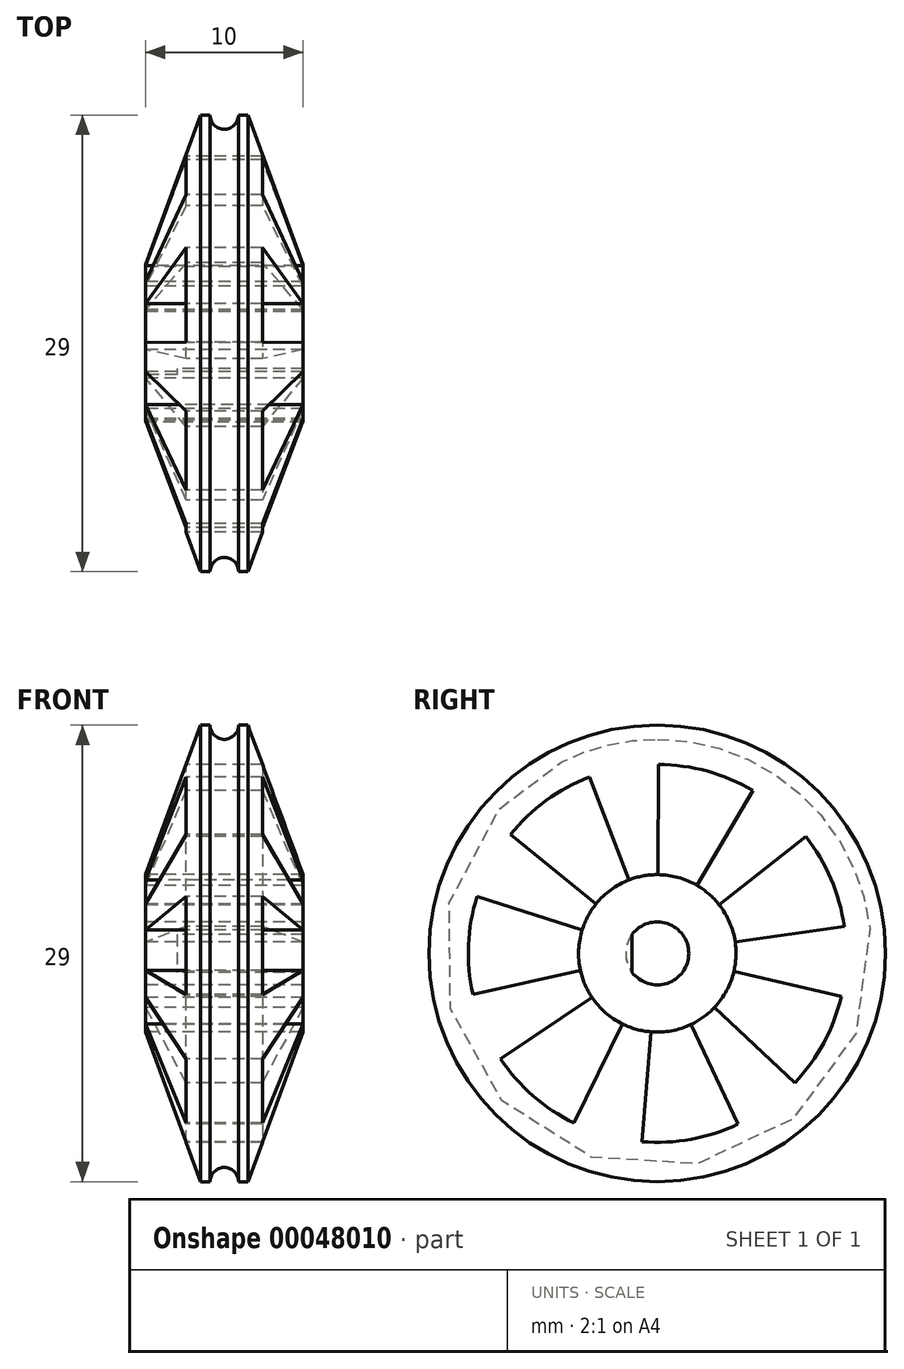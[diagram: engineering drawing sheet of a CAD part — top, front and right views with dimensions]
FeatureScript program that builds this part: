
annotation { "Feature Type Name" : "Feature", "Feature Type Description" : "" }
export const myFeature = defineFeature(function(context is Context, id is Id, definition is map)
    precondition{}
    {
        {
            var Q0;
            Q0=qCreatedBy(makeId("Front.planeOp"),FACE);
            var sketch = newSketch(context, id + "F0", { "sketchPlane" : qUnion([Q0])});
            skLineSegment(sketch, "E0.bottom", {"start": v(0, 0) * mm, "end": v(10, 0) * mm});
            skLineSegment(sketch, "E0.top", {"start": v(0, 5) * mm, "end": v(10, 5) * mm});
            skLineSegment(sketch, "E0.left", {"start": v(0, 0) * mm, "end": v(0, 5) * mm});
            skLineSegment(sketch, "E0.right", {"start": v(10, 0) * mm, "end": v(10, 5) * mm});
            skLineSegment(sketch, "E1", {"start": v(0, 5) * mm, "end": v(3.5, 14.5) * mm});
            skLineSegment(sketch, "E2", {"start": v(3.5, 14.5) * mm, "end": v(4.1, 14.5) * mm});
            skLineSegment(sketch, "E3", {"start": v(6.5, 14.5) * mm, "end": v(10, 5) * mm});
            skArc(sketch, "E4", {"start": v(4.1, 14.5) * mm, "mid": v(5, 13.6) * mm, "end": v(5.9, 14.5) * mm});
            skLineSegment(sketch, "E5.trimOffspring", {"start": v(5.9, 14.5) * mm, "end": v(6.5, 14.5) * mm});
            skLineSegment(sketch, "E6", {"start": v(4.1, 14.5) * mm, "end": v(5.9, 14.5) * mm, "construction": true});
            skSolve(sketch);
        }
        {
            var Q0;
            Q0 = qSketchRegion(id + "F0", true);
            var Q1;
            Q1=sQuery(id+"F0.wireOp",EDGE,"E0.bottom");
            revolve(context, id + "F1", {"entities" : qUnion([Q0]), "axis" : qUnion([Q1]), "revolveType" : RevolveType.FULL});
        }
        {
            var Q0;
            Q0=qCreatedBy(makeId("Right.planeOp"),FACE);
            var sketch = newSketch(context, id + "F2", { "sketchPlane" : qUnion([Q0])});
            skCircle(sketch, "E7", {"center": v(0, 0) * mm, "radius": 2 * mm});
            skSolve(sketch);
        }
        {
            var Q0;
            Q0=makeQuery(id+"F2.imprint","IMPRINT",FACE,{"disambiguationData":[TD([[makeQuery(id+"F2.imprint","IMPRINT",EDGE,{"derivedFrom":sQuery(id+"F2.wireOp",EDGE,"E7")}),1.0]])]});
            extrude(context, id + "F3", {"entities" : qUnion([Q0]), "operationType" : NewBodyOperationType.REMOVE, "depth" : 2 * mm});
        }
        {
            var Q0;
            Q0=makeQuery(id+"F1.opRevolve","SWEPT_FACE",FACE,{"disambiguationData":[OSD([sQuery(id+"F0.wireOp",EDGE,"E0.left")])]});
            var sketch = newSketch(context, id + "F4", { "sketchPlane" : qUnion([Q0])});
            skLineSegment(sketch, "E8", {"start": v(1.6, -1.2) * mm, "end": v(1.6, 1.2) * mm});
            skArc(sketch, "E9", {"start": v(1.6, 1.2) * mm, "mid": v(-2, 0) * mm, "end": v(1.6, -1.2) * mm});
            skArc(sketch, "E10", {"start": v(1.6, -1.2) * mm, "mid": v(2, 0) * mm, "end": v(1.6, 1.2) * mm, "construction": true});
            skArc(sketch, "E11", {"start": v(-2.14, -4.52) * mm, "mid": v(-0.9, -4.92) * mm, "end": v(0.4, -4.98) * mm});
            skArc(sketch, "E12", {"start": v(-5.14, -10.84) * mm, "mid": v(-2.15, -11.8) * mm, "end": v(0.97, -11.96) * mm});
            skLineSegment(sketch, "E13", {"start": v(-2.14, -4.52) * mm, "end": v(-5.14, -10.84) * mm});
            skLineSegment(sketch, "E14", {"start": v(0.4, -4.98) * mm, "end": v(0.97, -11.96) * mm});
            skLineSegment(sketch, "E15", {"start": v(-2.14, -4.52) * mm, "end": v(0, 0) * mm, "construction": true});
            skLineSegment(sketch, "E16", {"start": v(0, 0) * mm, "end": v(0.4, -4.98) * mm, "construction": true});
            skArc(sketch, "E17.1.0", {"start": v(2.2, -4.5) * mm, "mid": v(3.29, -3.77) * mm, "end": v(4.15, -2.79) * mm});
            skLineSegment(sketch, "E17.1.1", {"start": v(2.2, -4.5) * mm, "end": v(5.28, -10.78) * mm});
            skArc(sketch, "E17.1.2", {"start": v(5.28, -10.78) * mm, "mid": v(7.89, -9.05) * mm, "end": v(9.96, -6.7) * mm});
            skLineSegment(sketch, "E17.1.3", {"start": v(4.15, -2.79) * mm, "end": v(9.96, -6.7) * mm});
            skArc(sketch, "E17.2.0", {"start": v(4.88, -1.08) * mm, "mid": v(5, 0.22) * mm, "end": v(4.77, 1.5) * mm});
            skLineSegment(sketch, "E17.2.1", {"start": v(4.88, -1.08) * mm, "end": v(11.72, -2.6) * mm});
            skArc(sketch, "E17.2.2", {"start": v(11.72, -2.6) * mm, "mid": v(11.99, 0.53) * mm, "end": v(11.44, 3.61) * mm});
            skLineSegment(sketch, "E17.2.3", {"start": v(4.77, 1.5) * mm, "end": v(11.44, 3.61) * mm});
            skArc(sketch, "E17.3.0", {"start": v(3.89, 3.14) * mm, "mid": v(2.94, 4.04) * mm, "end": v(1.8, 4.67) * mm});
            skLineSegment(sketch, "E17.3.1", {"start": v(3.89, 3.14) * mm, "end": v(9.33, 7.54) * mm});
            skArc(sketch, "E17.3.2", {"start": v(9.33, 7.54) * mm, "mid": v(7.06, 9.7) * mm, "end": v(4.31, 11.2) * mm});
            skLineSegment(sketch, "E17.3.3", {"start": v(1.8, 4.67) * mm, "end": v(4.31, 11.2) * mm});
            skArc(sketch, "E17.4.0", {"start": v(-0.03, 5) * mm, "mid": v(-1.33, 4.82) * mm, "end": v(-2.53, 4.31) * mm});
            skLineSegment(sketch, "E17.4.1", {"start": v(-0.03, 5) * mm, "end": v(-0.08, 12) * mm});
            skArc(sketch, "E17.4.2", {"start": v(-0.08, 12) * mm, "mid": v(-3.18, 11.57) * mm, "end": v(-6.07, 10.35) * mm});
            skLineSegment(sketch, "E17.4.3", {"start": v(-2.53, 4.31) * mm, "end": v(-6.07, 10.35) * mm});
            skArc(sketch, "E17.5.0", {"start": v(-3.93, 3.1) * mm, "mid": v(-4.6, 1.97) * mm, "end": v(-4.95, 0.71) * mm});
            skLineSegment(sketch, "E17.5.1", {"start": v(-3.93, 3.1) * mm, "end": v(-9.43, 7.42) * mm});
            skArc(sketch, "E17.5.2", {"start": v(-9.43, 7.42) * mm, "mid": v(-11.03, 4.73) * mm, "end": v(-11.88, 1.71) * mm});
            skLineSegment(sketch, "E17.5.3", {"start": v(-4.95, 0.71) * mm, "end": v(-11.88, 1.71) * mm});
            skArc(sketch, "E17.6.0", {"start": v(-4.87, -1.14) * mm, "mid": v(-4.4, -2.36) * mm, "end": v(-3.64, -3.42) * mm});
            skLineSegment(sketch, "E17.6.1", {"start": v(-4.87, -1.14) * mm, "end": v(-11.68, -2.75) * mm});
            skArc(sketch, "E17.6.2", {"start": v(-11.68, -2.75) * mm, "mid": v(-10.57, -5.68) * mm, "end": v(-8.74, -8.22) * mm});
            skLineSegment(sketch, "E17.6.3", {"start": v(-3.64, -3.42) * mm, "end": v(-8.74, -8.22) * mm});
            skSolve(sketch);
        }
        {
            var Q0;
            Q0 = qSketchRegion(id + "F4", true);
            extrude(context, id + "F5", {"entities" : qUnion([Q0]), "operationType" : NewBodyOperationType.REMOVE, "oppositeDirection" : true, "depth" : 25 * mm});
        }
    });
